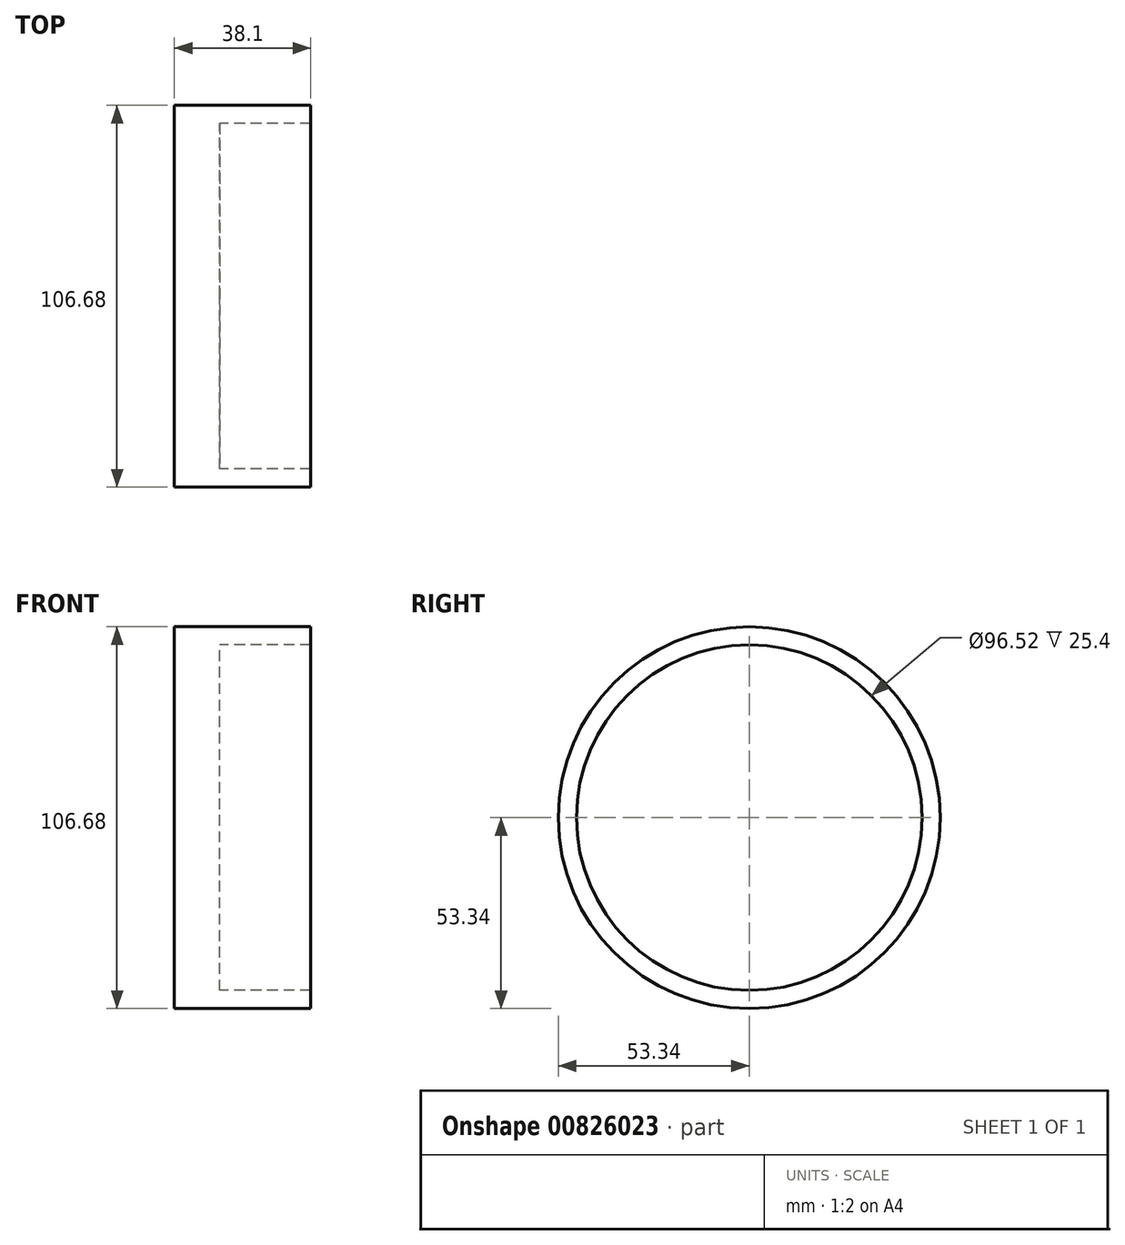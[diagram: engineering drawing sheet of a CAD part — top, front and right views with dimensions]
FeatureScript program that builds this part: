
annotation { "Feature Type Name" : "Feature", "Feature Type Description" : "" }
export const myFeature = defineFeature(function(context is Context, id is Id, definition is map)
    precondition{}
    {
        {
            var Q0;
            Q0=qCreatedBy(makeId("Right.planeOp"),FACE);
            var sketch = newSketch(context, id + "F0", { "sketchPlane" : qUnion([Q0])});
            skCircle(sketch, "E0", {"center": v(0, 0) * mm, "radius": 53.34 * mm});
            skCircle(sketch, "E1", {"center": v(0, 0) * mm, "radius": 48.26 * mm});
            skSolve(sketch);
        }
        {
            var Q0;
            Q0=makeQuery(id+"F0.imprint","IMPRINT",FACE,{"disambiguationData":[TD([[makeQuery(id+"F0.imprint","IMPRINT",EDGE,{"derivedFrom":sQuery(id+"F0.wireOp",EDGE,"E0")}),1.0]])]});
            var Q1;
            Q1=makeQuery(id+"F0.imprint","IMPRINT",FACE,{"disambiguationData":[TD([[makeQuery(id+"F0.imprint","IMPRINT",EDGE,{"derivedFrom":sQuery(id+"F0.wireOp",EDGE,"E1")}),1.0]])]});
            extrude(context, id + "F1", {"entities" : qUnion([Q0, Q1]), "oppositeDirection" : true, "depth" : 12.7 * mm, "offsetDistance" : 25.4 * mm});
        }
        {
            var Q0;
            Q0=makeQuery(id+"F0.imprint","IMPRINT",FACE,{"disambiguationData":[TD([[makeQuery(id+"F0.imprint","IMPRINT",EDGE,{"derivedFrom":sQuery(id+"F0.wireOp",EDGE,"E0")}),1.0]])]});
            extrude(context, id + "F2", {"entities" : qUnion([Q0]), "operationType" : NewBodyOperationType.ADD, "depth" : 25.4 * mm, "offsetDistance" : 25.4 * mm});
        }
    });
